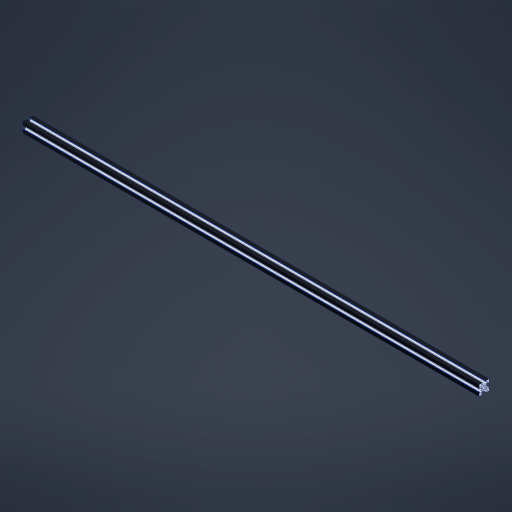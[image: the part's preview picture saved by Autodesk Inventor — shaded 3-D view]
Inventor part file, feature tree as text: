
AUTODESK INVENTOR PART (.ipt)
format: ipt  version: 2024.2 (Build 282272000, 272)  size: 317,440 bytes
history: native  units: mm
features: extrude x1, sketch x1
ambient origin geometry x8: Origin, YZ Plane, XZ Plane, XY Plane, X Axis, Y Axis, Z Axis, Center Point
bodies: Solid1 (feature_tree)
feature tree (2):
  extrude  "Extrusion1"  Depth=0.5mm
  sketch  "Sketch1"  dims[d2=6.5mm d3=0.5mm d4=4.0mm d5=3.465mm d6=5.48mm d7=0.795mm d8=0.305mm d9=2.95mm d11=0.75mm d14=45.0deg d15=10.0mm d16=1.0mm d17=3.0mm d18=45.0deg d19=40.0mm d21=360.0deg d23=900.0mm d24=0.0mm]
